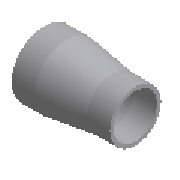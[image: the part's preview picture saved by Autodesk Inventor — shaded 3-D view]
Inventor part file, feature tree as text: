
AUTODESK INVENTOR PART (.ipt)
format: ipt  version: 2023.1 (Build 271208000, 208)  size: 166,400 bytes
history: native  units: mm (DEFAULTED — no unit token found)
features: other x4, revolve x1, sketch x1
ambient origin geometry x8: Origin, YZ Plane, XZ Plane, XY Plane, X Axis, Y Axis, Z Axis, Center Point
bodies: Solid1 (feature_tree)
feature tree (6):
  revolve  "Revolution1"  [1 undecoded]
  other  "Work Axis1"
  other  "Work Point1"
  other  "Work Axis2"
  other  "Work Point2"
  sketch  "Sketch1"  dims[d0=33.7mm d1=26.9mm d2=2.0mm d3=1.6mm d4=50.0mm d5=12.5mm d6=12.5mm d9=90.0deg d10=2.0mm]
note: 1 required parameter value undecoded (feature->parameter linkage not recoverable at this tier; creation-order binding heuristic only, values carry confidence <= 0.55)
